# Revit family: NTB-500
name_source: partatom
category: Plumbing Fixtures
units: mm (PartAtom-declared; Revit-internal decimal feet)

## family parameters
Always vertical = Yes
Cut with Voids When Loaded = Yes
Enable Cutting in Views = No
Maintain Annotation Orientation = No
OmniClass Number = 23.45.00.00
OmniClass Title = Sanitary, Laundry, and Cleaning Equipment
Part Type = Normal
Room Calculation Point = No
Round Connector Dimension = Use Diameter
Shared = No
Work Plane-Based = No

## types (2) — shared parameters
Default Elevation = 0"
Manufacturer = MIFAB
Material = Polyethylene, High Density
Width = 33 1/2"
array = 2

## per-type parameters (varying)
| type | Description | Ext End | Height of Body | Model | Pipe RP | Top RP 1 | URL | Void 1 TL | center void | center void h | pipe height |
| BIG-1150 | 1150lb. Big Max Grease Interceptor | -20" | 50" | XL-MI-G-PL-1150 | 38" | 19" | www,mifab.com | 12" | 10" | 4 1/4" | 12 1/2" |
| BIG-750 | 750lb. Big Max Grease Interceptor | -16" | 37" | XL-MI-G-PL-750 | 25 1/2" | 14" | www.mifab.com | 8" | 2" | 2" | 12 3/4" |

## geometry (parser evidence)
native form markers: Sweep x5
no freeform markers — native parametric forms only
